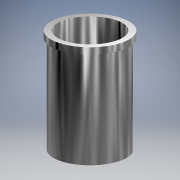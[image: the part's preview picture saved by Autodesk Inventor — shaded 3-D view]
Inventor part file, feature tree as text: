
AUTODESK INVENTOR PART (.ipt)
format: ipt  version: 2018 (Build 220112000, 112)  size: 118,784 bytes
history: native  units: mm
features: revolve x1, sketch x1
ambient origin geometry x8: Origin, YZ Plane, XZ Plane, XY Plane, X Axis, Y Axis, Z Axis, Center Point
bodies: Solid1 (feature_tree)
feature tree (2):
  revolve  "Revolution1"  [1 undecoded]
  sketch  "Sketch1"  dims[d0=40.0mm d1=13.5mm d2=12.0mm d3=14.5mm d4=2.5mm d5=90.0deg]
note: 1 required parameter value undecoded (feature->parameter linkage not recoverable at this tier; creation-order binding heuristic only, values carry confidence <= 0.55)
